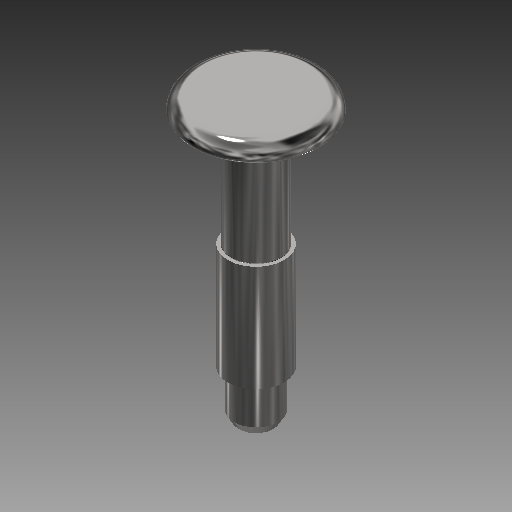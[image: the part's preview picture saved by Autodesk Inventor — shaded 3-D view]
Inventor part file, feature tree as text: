
AUTODESK INVENTOR PART (.ipt)
format: ipt  version: 2019 (Build 230136000, 136)  size: 164,864 bytes
history: native  units: mm
features: fillet x2, revolve x1, sketch x1
ambient origin geometry x8: Origin, YZ Plane, XZ Plane, XY Plane, X Axis, Y Axis, Z Axis, Center Point
bodies: Solid1 (feature_tree)
feature tree (4):
  revolve  "Revolution1"  [1 undecoded]
  fillet  "Fillet1"  Radius=15.0mm
  fillet  "Fillet2"  Radius=1.2mm
  sketch  "Sketch1"  dims[d1=2.5mm d2=16.0mm d3=15.0mm d4=1.2mm d5=60.0deg d6=3.125mm d7=3.5mm d8=4.0mm d9=9.0mm d10=0.5mm d11=2.0mm d12=1.75mm d15=40.0mm d16=90.0deg d17=0.1mm d18=0.25mm]
note: 1 required parameter value undecoded (feature->parameter linkage not recoverable at this tier; creation-order binding heuristic only, values carry confidence <= 0.55)
